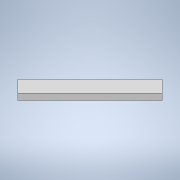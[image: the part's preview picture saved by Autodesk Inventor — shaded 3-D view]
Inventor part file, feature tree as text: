
AUTODESK INVENTOR PART (.ipt)
format: ipt  version: 2020.2 (Build 242310000, 310)  size: 93,696 bytes
history: native  units: in
note: dims shown in document units (in); Inventor stores cm internally (conversion verified against a paired STEP export)
features: extrude x1, sketch x1
ambient origin geometry x8: Origin, YZ Plane, XZ Plane, XY Plane, X Axis, Y Axis, Z Axis, Center Point
bodies: Solid1 (feature_tree)
feature tree (2):
  extrude  "Extrusion1"  TaperAngle=135.0deg  [1 undecoded]
  sketch  "Sketch1"  dims[d0=6.0in d1=135.0deg d2=1.0in d3=0.375in d4=0.0in]
note: 1 required parameter value undecoded (feature->parameter linkage not recoverable at this tier; creation-order binding heuristic only, values carry confidence <= 0.55)
